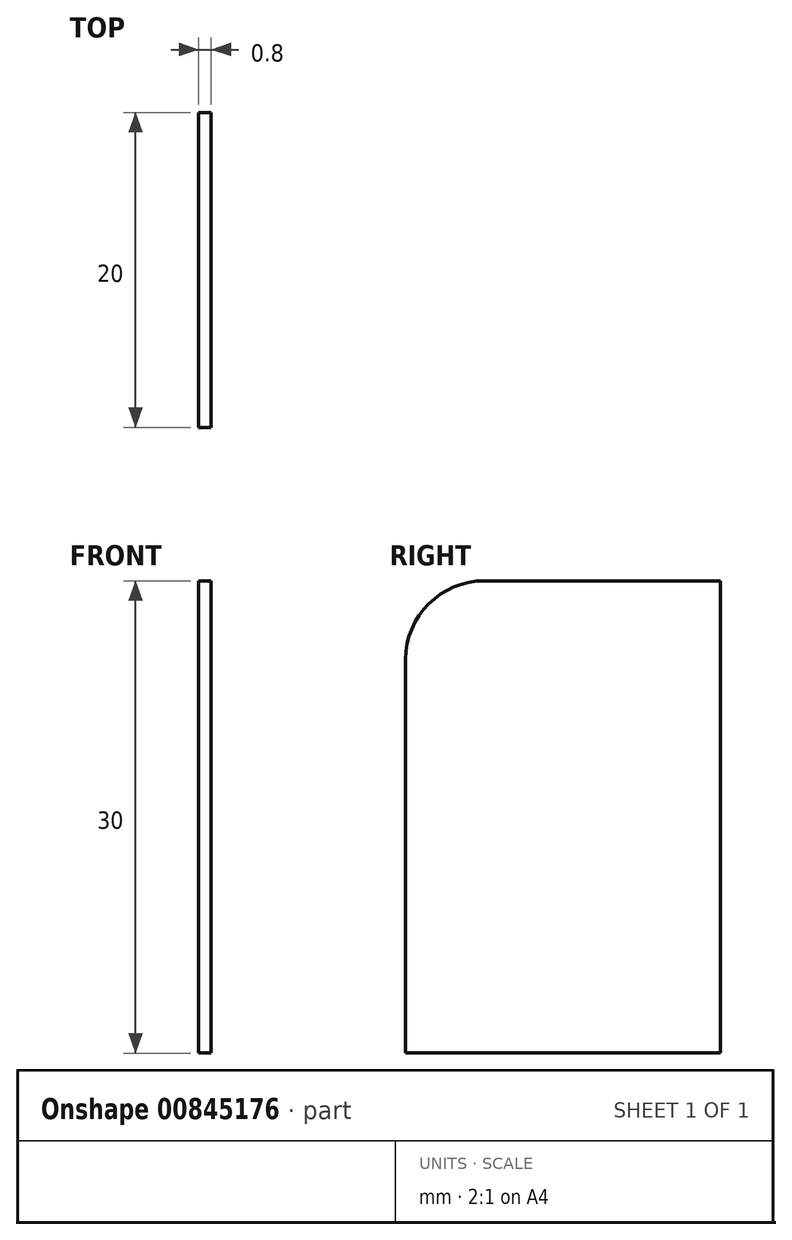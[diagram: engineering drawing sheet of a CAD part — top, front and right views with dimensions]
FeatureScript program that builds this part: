
annotation { "Feature Type Name" : "Feature", "Feature Type Description" : "" }
export const myFeature = defineFeature(function(context is Context, id is Id, definition is map)
    precondition{}
    {
        {
            var Q0;
            Q0=qCreatedBy(makeId("Right.planeOp"),FACE);
            var sketch = newSketch(context, id + "F0", { "sketchPlane" : qUnion([Q0])});
            skLineSegment(sketch, "E0", {"start": v(-5, 15.84) * mm, "end": v(-5, -9.16) * mm});
            skLineSegment(sketch, "E1", {"start": v(-5, -9.16) * mm, "end": v(15, -9.16) * mm});
            skLineSegment(sketch, "E2", {"start": v(15, -9.16) * mm, "end": v(15, 20.84) * mm});
            skLineSegment(sketch, "E3", {"start": v(15, 20.84) * mm, "end": v(0, 20.84) * mm});
            skArc(sketch, "E4", {"start": v(0, 20.84) * mm, "mid": v(-3.54, 19.38) * mm, "end": v(-5, 15.84) * mm});
            skSolve(sketch);
        }
        {
            var Q0;
            Q0=makeQuery(id+"F0.imprint","IMPRINT",FACE,{"disambiguationData":[TD([[makeQuery(id+"F0.imprint","IMPRINT",EDGE,{"derivedFrom":sQuery(id+"F0.wireOp",EDGE,"E0")}),1.0]])]});
            extrude(context, id + "F1", {"entities" : qUnion([Q0]), "depth" : 0.8 * mm, "offsetDistance" : 25 * mm});
        }
    });
